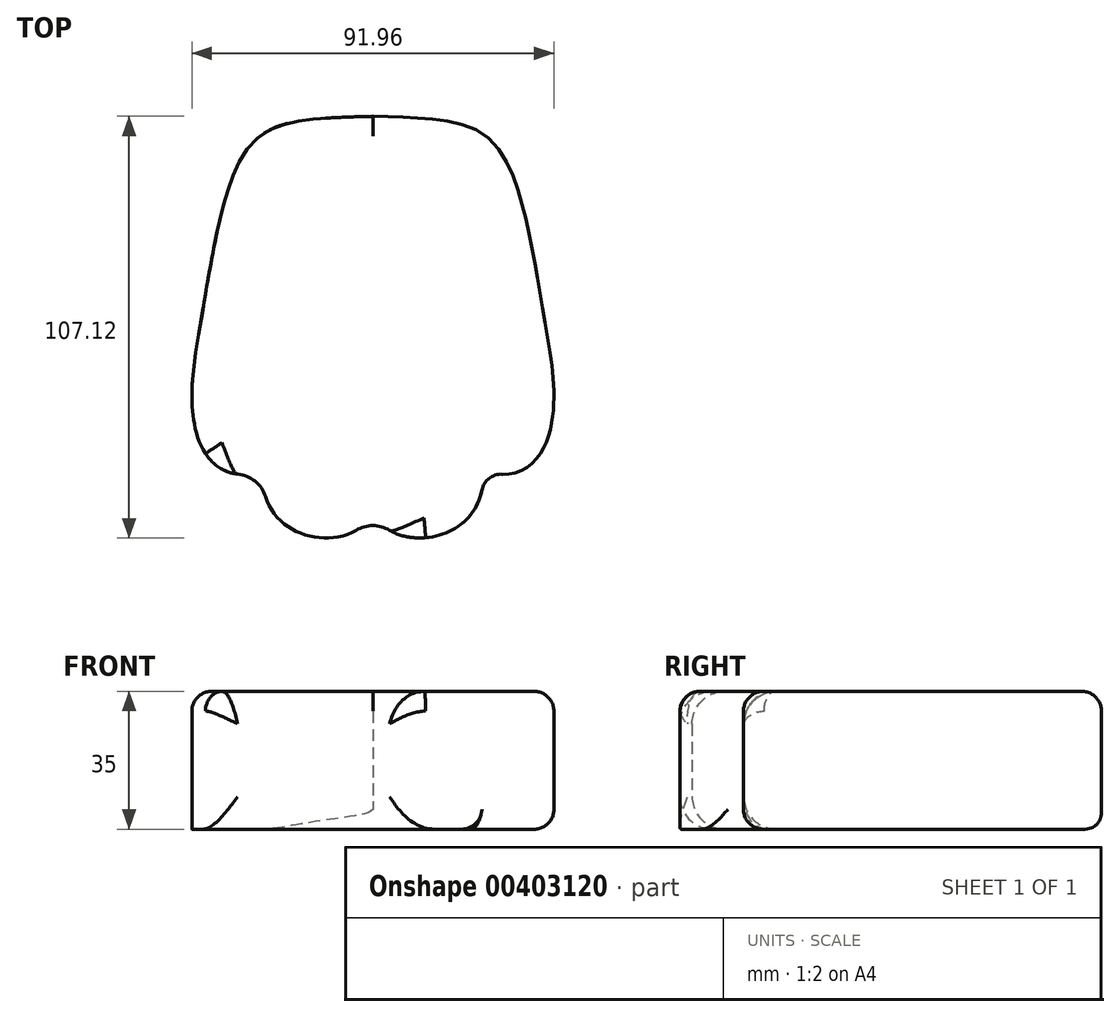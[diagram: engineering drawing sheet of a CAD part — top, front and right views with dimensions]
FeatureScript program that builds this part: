
annotation { "Feature Type Name" : "Feature", "Feature Type Description" : "" }
export const myFeature = defineFeature(function(context is Context, id is Id, definition is map)
    precondition{}
    {
        {
            var Q0;
            Q0=qCreatedBy(makeId("Top.planeOp"),FACE);
            var sketch = newSketch(context, id + "F0", { "sketchPlane" : qUnion([Q0])});
            skLineSegment(sketch, "E0.bottom", {"start": v(-60, 50) * mm, "end": v(0, 50) * mm, "construction": true});
            skLineSegment(sketch, "E0.top", {"start": v(-60, 0) * mm, "end": v(0, 0) * mm, "construction": true});
            skLineSegment(sketch, "E0.left", {"start": v(-60, 50) * mm, "end": v(-60, 0) * mm, "construction": true});
            skLineSegment(sketch, "E0.right", {"start": v(0, 50) * mm, "end": v(0, 0) * mm, "construction": true});
            skLineSegment(sketch, "E1", {"start": v(-30, 50) * mm, "end": v(-30, 0) * mm, "construction": true});
            skFitSpline(sketch, "E2", {"points": [v(-30, 60) * mm, v(-75, 0) * mm], "startDerivative": vector(-103.54, -2.78) * mm, "endDerivative": vector(-28.8, -177.22) * mm});
            skFitSpline(sketch, "E3", {"points": [v(-75, 0) * mm, v(-57.9, -28.72) * mm], "startDerivative": vector(-16.8, -103.46) * mm, "endDerivative": vector(7.75, 12.96) * mm});
            skFitSpline(sketch, "E4", {"points": [v(-57.9, -28.72) * mm, v(-30, -37.9) * mm], "startDerivative": vector(-7.75, -66.73) * mm, "endDerivative": vector(0, 41.6) * mm});
            skFitSpline(sketch, "E5.MirrorCS", {"points": [v(-2.1, -28.72) * mm, v(-30, -37.9) * mm], "startDerivative": vector(7.75, -66.73) * mm, "endDerivative": vector(0, 41.6) * mm});
            skFitSpline(sketch, "E6.MirrorCS", {"points": [v(15, 0) * mm, v(-2.1, -28.72) * mm], "startDerivative": vector(16.8, -103.46) * mm, "endDerivative": vector(-7.75, 12.96) * mm});
            skFitSpline(sketch, "E7.MirrorCS", {"points": [v(-30, 60) * mm, v(15, 0) * mm], "startDerivative": vector(103.54, -2.78) * mm, "endDerivative": vector(28.8, -177.22) * mm});
            skSolve(sketch);
        }
        {
            var Q0;
            Q0 = qSketchRegion(id + "F0", true);
            extrude(context, id + "F1", {"entities" : qUnion([Q0]), "depth" : 35 * mm});
        }
        {
            var Q0;
            Q0=makeQuery(id+"F1.opExtrude","SWEPT_FACE",FACE,{"disambiguationData":[OSD([sQuery(id+"F0.wireOp",EDGE,"E4")])]});
            fillet(context, id + "F2", {"entities" : qUnion([Q0]), "radius" : 8.25 * mm, "tangentPropagation" : true, "allowEdgeOverflow" : false});
        }
        {
            var Q0;
            Q0=makeQuery(id+"F1.opExtrude","SWEPT_FACE",FACE,{"disambiguationData":[OSD([sQuery(id+"F0.wireOp",EDGE,"E6.MirrorCS")])]});
            var Q1;
            {var subQ0=sQuery(id+"F0.wireOp",EDGE,"E4");Q1=makeQuery(id+"F2.opFillet","BLEND_FACE",FACE,{"disambiguationData":[OSD([subQ0]),TDD([makeQuery(id+"F1.opExtrude","CAP_EDGE",EDGE,{"disambiguationData":[OSD([subQ0])],"isStart":false})])]});}
            fillet(context, id + "F3", {"entities" : qUnion([Q0, Q1]), "radius" : 5 * mm, "tangentPropagation" : true, "allowEdgeOverflow" : false});
        }
    });
